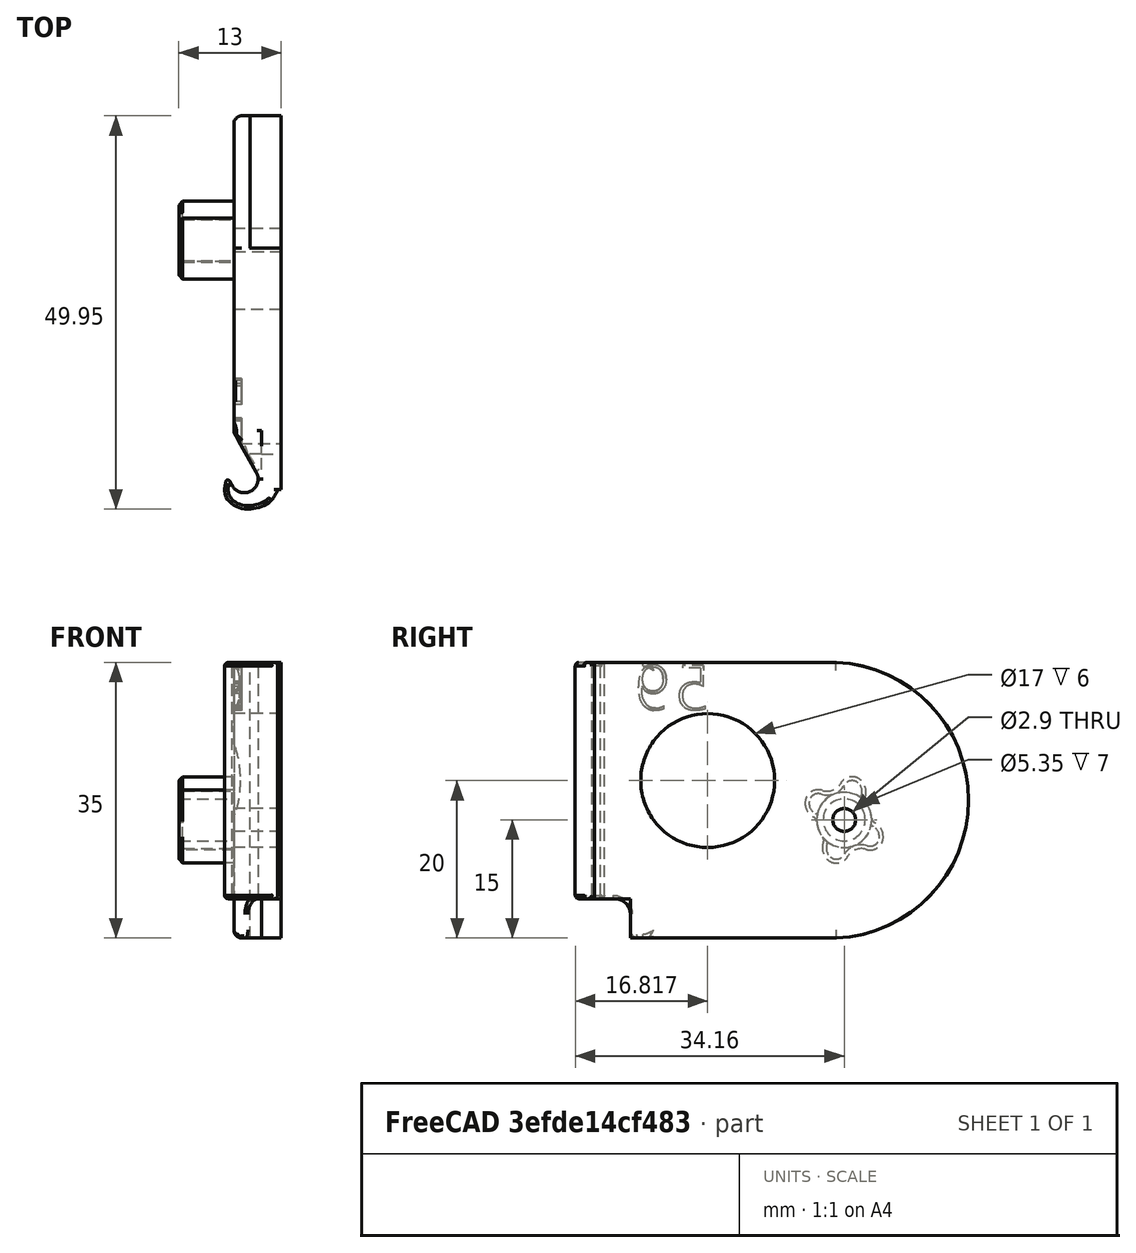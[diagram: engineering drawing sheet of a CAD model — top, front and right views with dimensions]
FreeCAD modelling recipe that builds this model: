
FCSTD DOCUMENT  (FreeCAD 0.18R)
Label: hinge-left-159deg-flat
License: All rights reserved
LicenseURL: http://en.wikipedia.org/wiki/All_rights_reserved
objects: App::FeaturePython×4, Part::FeaturePython×2, Part::Part2DObjectPython×1, Part::Extrusion×1, Part::Cut×1
note: 5 computed .brp shape members not serialized (recipe doc carries the construction recipe); baked Part::Feature solids carry a one-line shape summary decoded from their .brp

FEATURE [Part::FeaturePython] pillar_base_001  label="pillar-base_001"  # a2plus imported part (geometry in sourceFile) (typed FeaturePython)
  Placement = pos=(0.000608724,-0.981977,1.95002) rot=(-1,0,0;0.069988rad)
  a2p_Version = V0.1
  fixedPosition = false
  objectType = a2pPart
  sourceFile = ./parts/pillar-base.fcstd
  subassemblyImport = false
  timeLastImport = 1.60452e+09
  updateColors = true
FEATURE [Part::Part2DObjectPython] ShapeString  # Draft 2D object (typed FeaturePython)
  FontFile = <path>
  Placement = pos=(1.61,10.5,29) rot=(0.57735,-0.57735,-0.57735;2.0944rad)
  Size = 6
  String = 59
  Tracking = 0
FEATURE [Part::Extrusion] Extrude
  Base = -> ShapeString
  Dir = (-1,0,0)
  DirMode = 2
  FaceMakerClass = Part::FaceMakerBullseye
  LengthFwd = 2
  LengthRev = 0
  Solid = false
  Symmetric = false
FEATURE [Part::FeaturePython] bracket_left_flat_001  label="bracket-left-flat_001"  # a2plus imported part (geometry in sourceFile) (typed FeaturePython)
  a2p_Version = V0.1
  fixedPosition = true
  objectType = a2pPart
  sourceFile = ./parts/bracket-left-flat.fcstd
  subassemblyImport = false
  timeLastImport = 1.60454e+09
  updateColors = true
FEATURE [App::FeaturePython] axisCoincident_001  label="axisCoincident_001__bracket-left-flat_001"  # a2plus constraint (typed FeaturePython)
  Object1 = pillar_base_001
  Object2 = bracket_left_flat_001
  ParentTreeObject = -> pillar_base_001
  SubElement1 = Face17
  SubElement2 = Face48
  Suppressed = false
  Type = axial
  directionConstraint = 1
  lockRotation = false
FEATURE [App::FeaturePython] axisCoincident_001_mirror  label="axisCoincident_001__pillar-base_001"  # a2plus constraint (typed FeaturePython)
  Object1 = pillar_base_001
  Object2 = bracket_left_flat_001
  ParentTreeObject = -> bracket_left_flat_001
  SubElement1 = Face17
  SubElement2 = Face48
  Suppressed = false
  Type = axial
  directionConstraint = 1
  lockRotation = false
FEATURE [App::FeaturePython] planeCoincident_001  label="planeCoincident_001__bracket-left-flat_001"  # a2plus constraint (typed FeaturePython)
  Object1 = pillar_base_001
  Object2 = bracket_left_flat_001
  ParentTreeObject = -> pillar_base_001
  SubElement1 = Face1
  SubElement2 = Face72
  Suppressed = false
  Type = plane
  directionConstraint = 0
  offset = 0
FEATURE [App::FeaturePython] planeCoincident_001_mirror  label="planeCoincident_001__pillar-base_001"  # a2plus constraint (typed FeaturePython)
  Object1 = pillar_base_001
  Object2 = bracket_left_flat_001
  ParentTreeObject = -> bracket_left_flat_001
  SubElement1 = Face1
  SubElement2 = Face72
  Suppressed = false
  Type = plane
  directionConstraint = 0
  offset = 0
FEATURE [Part::Cut] Cut
  Base = -> bracket_left_flat_001
  Tool = -> Extrude
note: 1 file-system path scrubbed to <path> (originals preserved in the JSON sidecar)
